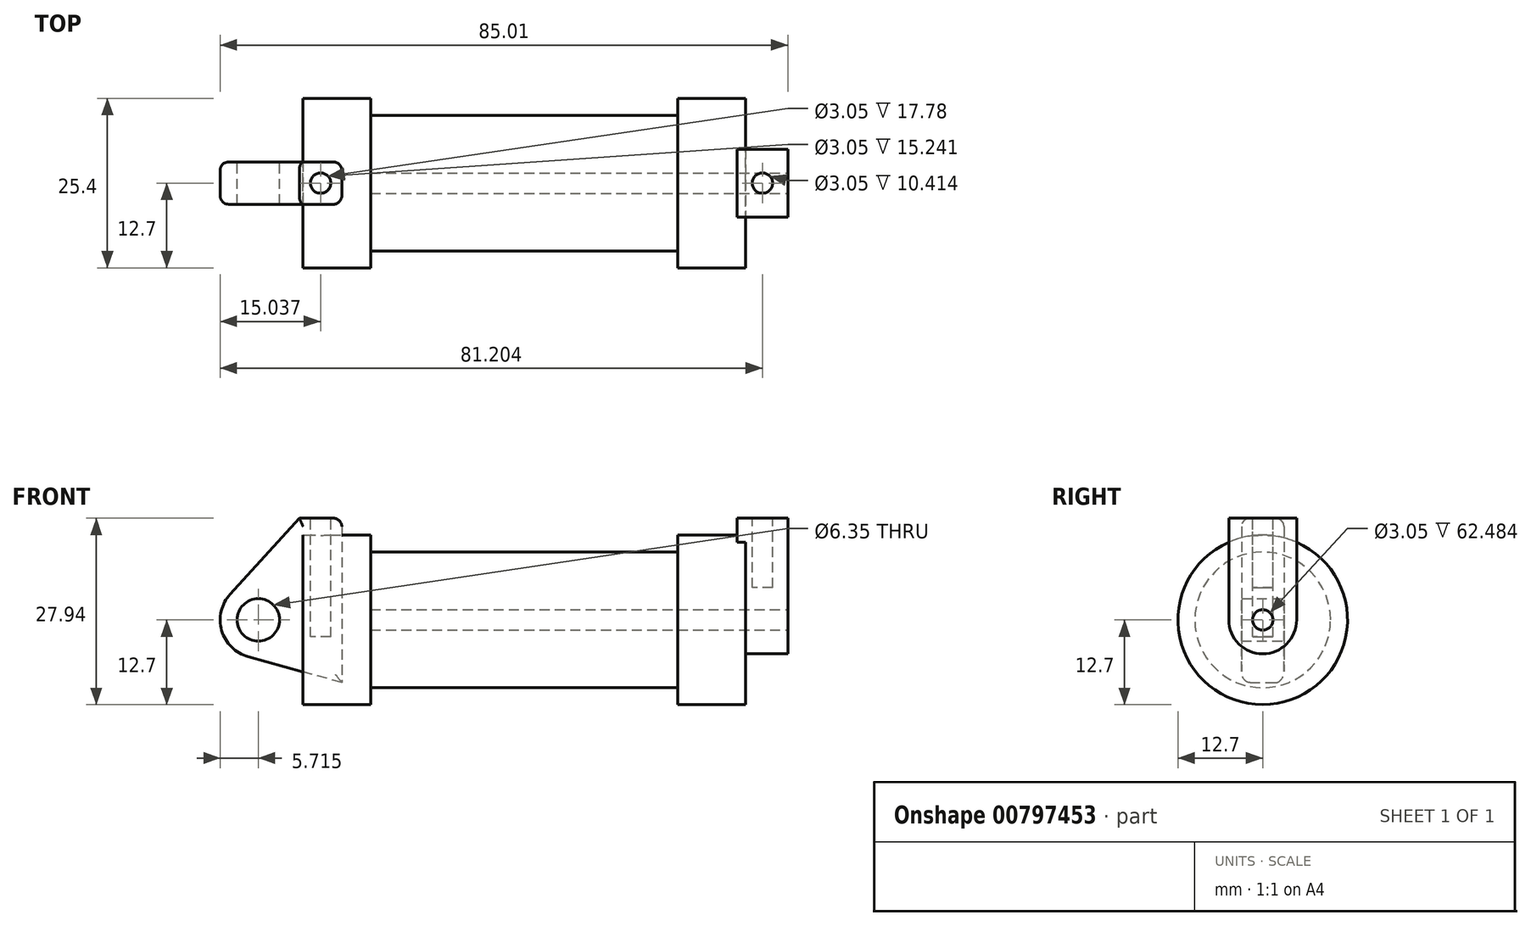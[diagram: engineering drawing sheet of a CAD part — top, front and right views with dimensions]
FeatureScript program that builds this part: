
annotation { "Feature Type Name" : "Feature", "Feature Type Description" : "" }
export const myFeature = defineFeature(function(context is Context, id is Id, definition is map)
    precondition{}
    {
        {
            var Q0;
            Q0=qCreatedBy(makeId("Front.planeOp"),FACE);
            var sketch = newSketch(context, id + "F0", { "sketchPlane" : qUnion([Q0])});
            skLineSegment(sketch, "E0", {"start": v(0, 0) * mm, "end": v(0, 12.7) * mm});
            skLineSegment(sketch, "E1", {"start": v(0, 12.7) * mm, "end": v(10.16, 12.7) * mm});
            skLineSegment(sketch, "E2", {"start": v(10.16, 12.7) * mm, "end": v(10.16, 10.16) * mm});
            skLineSegment(sketch, "E3", {"start": v(10.16, 10.16) * mm, "end": v(56.13, 10.16) * mm});
            skLineSegment(sketch, "E4", {"start": v(56.13, 10.16) * mm, "end": v(56.13, 12.7) * mm});
            skLineSegment(sketch, "E5", {"start": v(56.13, 12.7) * mm, "end": v(66.3, 12.7) * mm});
            skLineSegment(sketch, "E6", {"start": v(66.3, 12.7) * mm, "end": v(66.3, 0) * mm});
            skLineSegment(sketch, "E7", {"start": v(66.3, 0) * mm, "end": v(0, 0) * mm});
            skLineSegment(sketch, "E8", {"start": v(5.84, 15.24) * mm, "end": v(-0.5, 15.24) * mm});
            skLineSegment(sketch, "E9", {"start": v(-0.5, 15.24) * mm, "end": v(-10.88, 3.85) * mm});
            skLineSegment(sketch, "E10", {"start": v(0, 0) * mm, "end": v(-6.65, 0) * mm});
            skCircle(sketch, "E11", {"center": v(-6.65, 0) * mm, "radius": 5.72 * mm});
            skCircle(sketch, "E12", {"center": v(-6.65, 0) * mm, "radius": 3.18 * mm});
            skLineSegment(sketch, "E13", {"start": v(5.84, 15.24) * mm, "end": v(5.84, -9.4) * mm});
            skLineSegment(sketch, "E14", {"start": v(5.84, -9.4) * mm, "end": v(-8.18, -5.5) * mm});
            skSolve(sketch);
        }
        {
            var Q0;
            {var subQ0=sQuery(id+"F0.wireOp",EDGE,"E2");Q0=makeQuery(id+"F0.imprint","IMPRINT",FACE,{"disambiguationData":[TD([[makeQuery(id+"F0.imprint","IMPRINT",EDGE,{"derivedFrom":subQ0}),-1.0]])]});}
            var Q1;
            {var subQ0=sQuery(id+"F0.wireOp",EDGE,"E0");Q1=makeQuery(id+"F0.imprint","IMPRINT",FACE,{"disambiguationData":[TD([[makeQuery(id+"F0.imprint","IMPRINT",EDGE,{"derivedFrom":subQ0}),-1.0]])]});}
            var Q2;
            Q2=sQuery(id+"F0.wireOp",EDGE,"E7");
            revolve(context, id + "F1", {"surfaceOperationType" : NewSurfaceOperationType.NEW, "entities" : qUnion([Q0, Q1]), "axis" : qUnion([Q2]), "revolveType" : RevolveType.FULL});
        }
        {
            var Q0;
            {var subQ1=sQuery(id+"F0.wireOp",EDGE,"E0");Q0=makeQuery(id+"F0.imprint","IMPRINT",FACE,{"disambiguationData":[TD([[makeQuery(id+"F0.imprint","IMPRINT",EDGE,{"derivedFrom":subQ1}),1.0]])]});}
            var Q1;
            {var subQ5=sQuery(id+"F0.wireOp",EDGE,"E12");Q1=makeQuery(id+"F0.imprint","IMPRINT",FACE,{"disambiguationData":[TD([[makeQuery(id+"F0.imprint","IMPRINT",EDGE,{"derivedFrom":subQ5}),-1.0]])]});}
            var Q2;
            {var subQ0=sQuery(id+"F0.wireOp",EDGE,"E14");Q2=makeQuery(id+"F0.imprint","IMPRINT",FACE,{"disambiguationData":[TD([[makeQuery(id+"F0.imprint","IMPRINT",EDGE,{"derivedFrom":subQ0}),-1.0]])]});}
            var Q3;
            {var subQ0=sQuery(id+"F0.wireOp",EDGE,"E0");Q3=makeQuery(id+"F0.imprint","IMPRINT",FACE,{"disambiguationData":[TD([[makeQuery(id+"F0.imprint","IMPRINT",EDGE,{"derivedFrom":subQ0}),-1.0]])]});}
            extrude(context, id + "F2", {"entities" : qUnion([Q0, Q1, Q2, Q3]), "endBound" : BoundingType.SYMMETRIC, "depth" : 6.35 * mm, "offsetDistance" : 25.4 * mm});
        }
        {
            var Q0;
            Q0=makeQuery(id+"F1.opRevolve","SWEPT_FACE",FACE,{"disambiguationData":[OSD([sQuery(id+"F0.wireOp",EDGE,"E6")])]});
            var sketch = newSketch(context, id + "F3", { "sketchPlane" : qUnion([Q0])});
            skCircle(sketch, "E15", {"center": v(0, 0) * mm, "radius": 1.52 * mm});
            skCircle(sketch, "E16", {"center": v(0, 0) * mm, "radius": 5.08 * mm});
            skLineSegment(sketch, "E17", {"start": v(5.08, 0) * mm, "end": v(5.08, 15.24) * mm});
            skLineSegment(sketch, "E18.MirrorCS", {"start": v(-5.08, 0) * mm, "end": v(-5.08, 15.24) * mm});
            skLineSegment(sketch, "E19", {"start": v(5.08, 15.24) * mm, "end": v(-5.08, 15.24) * mm});
            skSolve(sketch);
        }
        {
            var Q0;
            {var subQ0=sQuery(id+"F3.wireOp",EDGE,"E19");Q0=makeQuery(id+"F3.imprint","IMPRINT",FACE,{"disambiguationData":[TD([[makeQuery(id+"F3.imprint","IMPRINT",EDGE,{"derivedFrom":subQ0}),1.0]])]});}
            var Q1;
            {var subQ0=sQuery(id+"F3.wireOp",EDGE,"E17");var subQ1=sQuery(id+"F3.wireOp",EDGE,"E16");var subQ2=makeQuery(id+"F3.imprint","INTERSECT",VERTEX,{"derivedFrom":[subQ1,subQ0]});Q1=makeQuery(id+"F3.imprint","IMPRINT",FACE,{"disambiguationData":[TD([[makeQuery(id+"F3.imprint","IMPRINT",EDGE,{"disambiguationData":[TD([[subQ2,-1.0]])],"derivedFrom":subQ1}),-1.0]])]});}
            var Q2;
            Q2=makeQuery(id+"F3.imprint","IMPRINT",FACE,{"disambiguationData":[TD([[makeQuery(id+"F3.imprint","IMPRINT",EDGE,{"derivedFrom":sQuery(id+"F3.wireOp",EDGE,"E15")}),-1.0]])]});
            extrude(context, id + "F4", {"entities" : qUnion([Q0, Q1, Q2]), "oppositeDirection" : true, "depth" : 1.27 * mm, "offsetDistance" : 25.4 * mm});
        }
        {
            var Q0;
            Q0=makeQuery(id+"F4.opExtrude","CAP_FACE",FACE,{"disambiguationData":[OSD([sQuery(id+"F3.wireOp",EDGE,"E16"),sQuery(id+"F3.wireOp",EDGE,"E17"),sQuery(id+"F3.wireOp",EDGE,"E18.MirrorCS"),sQuery(id+"F3.wireOp",EDGE,"E19")])],"isStart":true});
            extrude(context, id + "F5", {"entities" : qUnion([Q0]), "operationType" : NewBodyOperationType.ADD, "depth" : 6.35 * mm, "offsetDistance" : 25.4 * mm});
        }
        {
            var Q0;
            Q0=makeQuery(id+"F3.imprint","IMPRINT",FACE,{"disambiguationData":[TD([[makeQuery(id+"F3.imprint","IMPRINT",EDGE,{"derivedFrom":sQuery(id+"F3.wireOp",EDGE,"E15")}),1.0]])]});
            var Q1;
            Q1=makeQuery(id+"F1.opRevolve","SWEPT_FACE",FACE,{"disambiguationData":[OSD([sQuery(id+"F0.wireOp",EDGE,"E2")])]});
            extrude(context, id + "F6", {"entities" : qUnion([Q0]), "operationType" : NewBodyOperationType.REMOVE, "endBound" : BoundingType.UP_TO_SURFACE, "oppositeDirection" : true, "depth" : 25.4 * mm, "endBoundEntityFace" : qUnion([Q1]), "offsetDistance" : 25.4 * mm});
        }
        {
            var Q0;
            Q0=makeQuery(id+"F2.opExtrude","SWEPT_FACE",FACE,{"disambiguationData":[OSD([sQuery(id+"F0.wireOp",EDGE,"E8")])]});
            var sketch = newSketch(context, id + "F7", { "sketchPlane" : qUnion([Q0])});
            skLineSegment(sketch, "E20", {"start": v(-0.5, 3.18) * mm, "end": v(5.84, -3.18) * mm, "construction": true});
            skCircle(sketch, "E21", {"center": v(2.67, 0) * mm, "radius": 1.52 * mm});
            skSolve(sketch);
        }
        {
            var Q0;
            Q0=makeQuery(id+"F7.imprint","IMPRINT",FACE,{"disambiguationData":[TD([[makeQuery(id+"F7.imprint","IMPRINT",EDGE,{"derivedFrom":sQuery(id+"F7.wireOp",EDGE,"E21")}),1.0]])]});
            extrude(context, id + "F8", {"entities" : qUnion([Q0]), "operationType" : NewBodyOperationType.REMOVE, "oppositeDirection" : true, "depth" : 17.78 * mm, "offsetDistance" : 25.4 * mm});
        }
        {
            var Q0;
            {var subQ0=sQuery(id+"F3.wireOp",EDGE,"E19");Q0=makeQuery(id+"F5.boolean.opBoolean","MERGE",FACE,{"derivedFrom":[makeQuery(id+"F4.opExtrude","SWEPT_FACE",FACE,{"disambiguationData":[OSD([subQ0])]}),makeQuery(id+"F5.opExtrude","SWEPT_FACE",FACE,{"disambiguationData":[OSD([subQ0])]})]});}
            var sketch = newSketch(context, id + "F9", { "sketchPlane" : qUnion([Q0])});
            skLineSegment(sketch, "E22", {"start": v(65.02, 5.08) * mm, "end": v(72.64, -5.08) * mm, "construction": true});
            skCircle(sketch, "E23", {"center": v(68.83, 0) * mm, "radius": 1.52 * mm});
            skSolve(sketch);
        }
        {
            var Q0;
            Q0=makeQuery(id+"F9.imprint","IMPRINT",FACE,{"disambiguationData":[TD([[makeQuery(id+"F9.imprint","IMPRINT",EDGE,{"derivedFrom":sQuery(id+"F9.wireOp",EDGE,"E23")}),1.0]])]});
            extrude(context, id + "F10", {"entities" : qUnion([Q0]), "operationType" : NewBodyOperationType.REMOVE, "oppositeDirection" : true, "depth" : 10.4 * mm, "offsetDistance" : 25.4 * mm});
        }
        {
            var Q0;
            Q0=makeQuery(id+"F1.opRevolve","SWEPT_EDGE",EDGE,{"disambiguationData":[OSD([sQuery(id+"F0.wireOp",EDGE,"E1"),sQuery(id+"F0.wireOp",EDGE,"E2")])]});
            var Q1;
            Q1=makeQuery(id+"F2.opExtrude","SWEPT_EDGE",EDGE,{"disambiguationData":[OSD([sQuery(id+"F0.wireOp",EDGE,"E8"),sQuery(id+"F0.wireOp",EDGE,"E13")])]});
            var Q2;
            Q2=makeQuery(id+"F2.opExtrude","CAP_EDGE",EDGE,{"disambiguationData":[OSD([sQuery(id+"F0.wireOp",EDGE,"E8")])],"isStart":false});
            var Q3;
            Q3=makeQuery(id+"F2.opExtrude","CAP_EDGE",EDGE,{"disambiguationData":[OSD([sQuery(id+"F0.wireOp",EDGE,"E8")])],"isStart":true});
            var Q4;
            Q4=makeQuery(id+"F2.opExtrude","CAP_EDGE",EDGE,{"disambiguationData":[OSD([sQuery(id+"F0.wireOp",EDGE,"E9")])],"isStart":false});
            var Q5;
            Q5=makeQuery(id+"F2.opExtrude","CAP_EDGE",EDGE,{"disambiguationData":[OSD([sQuery(id+"F0.wireOp",EDGE,"E11")])],"isStart":false});
            var Q6;
            Q6=makeQuery(id+"F1.opRevolve","SWEPT_EDGE",EDGE,{"disambiguationData":[OSD([sQuery(id+"F0.wireOp",EDGE,"E2"),sQuery(id+"F0.wireOp",EDGE,"E3")])]});
            var Q7;
            Q7=makeQuery(id+"F1.opRevolve","SWEPT_EDGE",EDGE,{"disambiguationData":[OSD([sQuery(id+"F0.wireOp",EDGE,"E4"),sQuery(id+"F0.wireOp",EDGE,"E5")])]});
            var Q8;
            Q8=makeQuery(id+"F1.opRevolve","SWEPT_EDGE",EDGE,{"disambiguationData":[OSD([sQuery(id+"F0.wireOp",EDGE,"E5"),sQuery(id+"F0.wireOp",EDGE,"E6")])]});
            var Q9;
            Q9=makeQuery(id+"F5.opExtrude","CAP_EDGE",EDGE,{"disambiguationData":[OSD([sQuery(id+"F3.wireOp",EDGE,"E19")])],"isStart":false});
            var Q10;
            {var subQ0=sQuery(id+"F3.wireOp",EDGE,"E19");var subQ1=sQuery(id+"F3.wireOp",EDGE,"E17");Q10=makeQuery(id+"F5.boolean.opBoolean","MERGE",EDGE,{"derivedFrom":[makeQuery(id+"F4.opExtrude","SWEPT_EDGE",EDGE,{"disambiguationData":[OSD([subQ1,subQ0])]}),makeQuery(id+"F5.opExtrude","SWEPT_EDGE",EDGE,{"disambiguationData":[OSD([subQ1,subQ0])]})]});}
            var Q11;
            {var subQ0=sQuery(id+"F3.wireOp",EDGE,"E19");var subQ1=sQuery(id+"F3.wireOp",EDGE,"E18.MirrorCS");Q11=makeQuery(id+"F5.boolean.opBoolean","MERGE",EDGE,{"derivedFrom":[makeQuery(id+"F4.opExtrude","SWEPT_EDGE",EDGE,{"disambiguationData":[OSD([subQ1,subQ0])]}),makeQuery(id+"F5.opExtrude","SWEPT_EDGE",EDGE,{"disambiguationData":[OSD([subQ1,subQ0])]})]});}
            var Q12;
            Q12=makeQuery(id+"F5.opExtrude","CAP_EDGE",EDGE,{"disambiguationData":[OSD([sQuery(id+"F3.wireOp",EDGE,"E18.MirrorCS")])],"isStart":false});
            var Q13;
            {var subQ0=sQuery(id+"F3.wireOp",EDGE,"E16");Q13=makeQuery(id+"F5.boolean.opBoolean","MERGE",FACE,{"derivedFrom":[makeQuery(id+"F4.opExtrude","SWEPT_FACE",FACE,{"disambiguationData":[OSD([subQ0])]}),makeQuery(id+"F5.opExtrude","SWEPT_FACE",FACE,{"disambiguationData":[OSD([subQ0])]})]});}
            var Q14;
            Q14=makeQuery(id+"F1.opRevolve","SWEPT_FACE",FACE,{"disambiguationData":[OSD([sQuery(id+"F0.wireOp",EDGE,"E6")])]});
            var Q15;
            {var subQ0=sQuery(id+"F3.wireOp",EDGE,"E18.MirrorCS");Q15=makeQuery(id+"F5.boolean.opBoolean","MERGE",FACE,{"derivedFrom":[makeQuery(id+"F4.opExtrude","SWEPT_FACE",FACE,{"disambiguationData":[OSD([subQ0])]}),makeQuery(id+"F5.opExtrude","SWEPT_FACE",FACE,{"disambiguationData":[OSD([subQ0])]})]});}
            var Q16;
            Q16=makeQuery(id+"F2.opExtrude","CAP_EDGE",EDGE,{"disambiguationData":[OSD([sQuery(id+"F0.wireOp",EDGE,"E9")])],"isStart":true});
            var Q17;
            Q17=makeQuery(id+"F2.opExtrude","CAP_EDGE",EDGE,{"disambiguationData":[OSD([sQuery(id+"F0.wireOp",EDGE,"E13")])],"isStart":true});
            var Q18;
            Q18=makeQuery(id+"F2.opExtrude","CAP_EDGE",EDGE,{"disambiguationData":[OSD([sQuery(id+"F0.wireOp",EDGE,"E13")])],"isStart":false});
            var Q19;
            Q19=makeQuery(id+"F1.opRevolve","SWEPT_EDGE",EDGE,{"disambiguationData":[OSD([sQuery(id+"F0.wireOp",EDGE,"E3"),sQuery(id+"F0.wireOp",EDGE,"E4")])]});
            fillet(context, id + "F11", {"entities" : qUnion([Q0, Q1, Q2, Q3, Q4, Q5, Q6, Q7, Q8, Q9, Q10, Q11, Q12, Q13, Q14, Q15, Q16, Q17, Q18, Q19]), "radius" : 1.27 * mm, "tangentPropagation" : true, "allowEdgeOverflow" : false});
        }
    });
